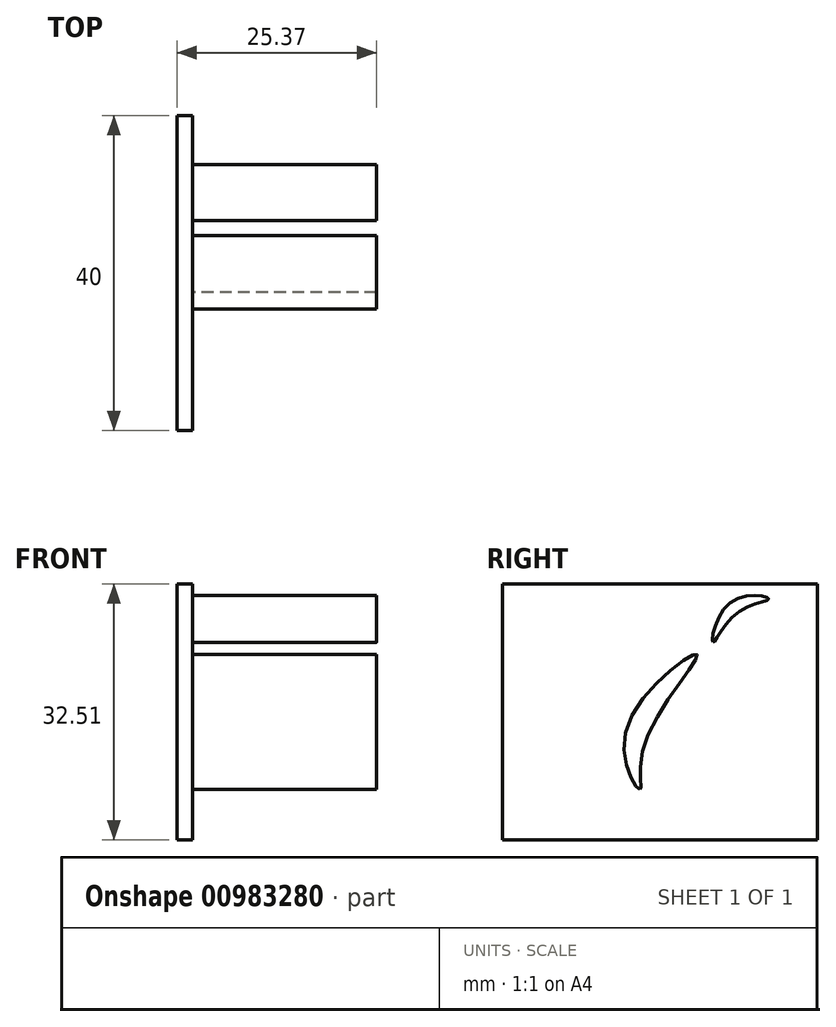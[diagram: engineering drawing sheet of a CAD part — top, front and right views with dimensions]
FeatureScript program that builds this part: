
annotation { "Feature Type Name" : "Feature", "Feature Type Description" : "" }
export const myFeature = defineFeature(function(context is Context, id is Id, definition is map)
    precondition{}
    {
        {
            var Q0;
            Q0=qCreatedBy(makeId("Top.planeOp"),FACE);
            var sketch = newSketch(context, id + "F0", { "sketchPlane" : qUnion([Q0])});
            skLineSegment(sketch, "E0.bottom", {"start": v(-30.33, 15.31) * mm, "end": v(-28.33, 15.31) * mm});
            skLineSegment(sketch, "E0.top", {"start": v(-30.33, -24.69) * mm, "end": v(-28.33, -24.69) * mm});
            skLineSegment(sketch, "E0.left", {"start": v(-30.33, 15.31) * mm, "end": v(-30.33, -24.69) * mm});
            skLineSegment(sketch, "E0.right", {"start": v(-28.33, 15.31) * mm, "end": v(-28.33, -24.69) * mm});
            skSolve(sketch);
        }
        {
            var Q0;
            Q0=makeQuery(id+"F0.imprint","IMPRINT",FACE,{"disambiguationData":[TD([[makeQuery(id+"F0.imprint","IMPRINT",EDGE,{"derivedFrom":sQuery(id+"F0.wireOp",EDGE,"E0.bottom")}),-1.0]])]});
            extrude(context, id + "F1", {"entities" : qUnion([Q0]), "depth" : 32.5 * mm, "offsetDistance" : 25.4 * mm});
        }
        {
            var Q0;
            Q0=makeQuery(id+"F1.opExtrude","SWEPT_FACE",FACE,{"disambiguationData":[OSD([sQuery(id+"F0.wireOp",EDGE,"E0.right")])]});
            var sketch = newSketch(context, id + "F2", { "sketchPlane" : qUnion([Q0])});
            skFitSpline(sketch, "E1", {"points": [v(-7.25, 6.4) * mm, v(-6.66, 12.12) * mm, v(0, 23.55) * mm, v(-9.02, 13.9) * mm, v(-7.25, 6.4) * mm]});
            skSolve(sketch);
        }
        {
            var Q0;
            Q0=makeQuery(id+"F2.imprint","IMPRINT",FACE,{"disambiguationData":[TD([[makeQuery(id+"F2.imprint","IMPRINT",EDGE,{"derivedFrom":sQuery(id+"F2.wireOp",EDGE,"E1")}),-1.0]])]});
            var sketch = newSketch(context, id + "F3", { "sketchPlane" : qUnion([Q0])});
            skFitSpline(sketch, "E2", {"points": [v(2.01, 25.12) * mm, v(5.16, 28.87) * mm, v(9.1, 30.64) * mm, v(4.38, 30.25) * mm, v(2.01, 25.12) * mm]});
            skSolve(sketch);
        }
        {
            var Q0;
            Q0=makeQuery(id+"F2.imprint","IMPRINT",FACE,{"disambiguationData":[TD([[makeQuery(id+"F2.imprint","IMPRINT",EDGE,{"derivedFrom":sQuery(id+"F2.wireOp",EDGE,"E1")}),1.0]])]});
            extrude(context, id + "F4", {"entities" : qUnion([Q0]), "operationType" : NewBodyOperationType.ADD, "depth" : 23.37 * mm, "offsetDistance" : 25.4 * mm});
        }
        {
            var Q0;
            Q0=makeQuery(id+"F3.imprint","IMPRINT",FACE,{"disambiguationData":[TD([[makeQuery(id+"F3.imprint","IMPRINT",EDGE,{"derivedFrom":sQuery(id+"F3.wireOp",EDGE,"E2")}),1.0]])]});
            extrude(context, id + "F5", {"entities" : qUnion([Q0]), "operationType" : NewBodyOperationType.ADD, "depth" : 23.37 * mm, "offsetDistance" : 25.4 * mm});
        }
    });
